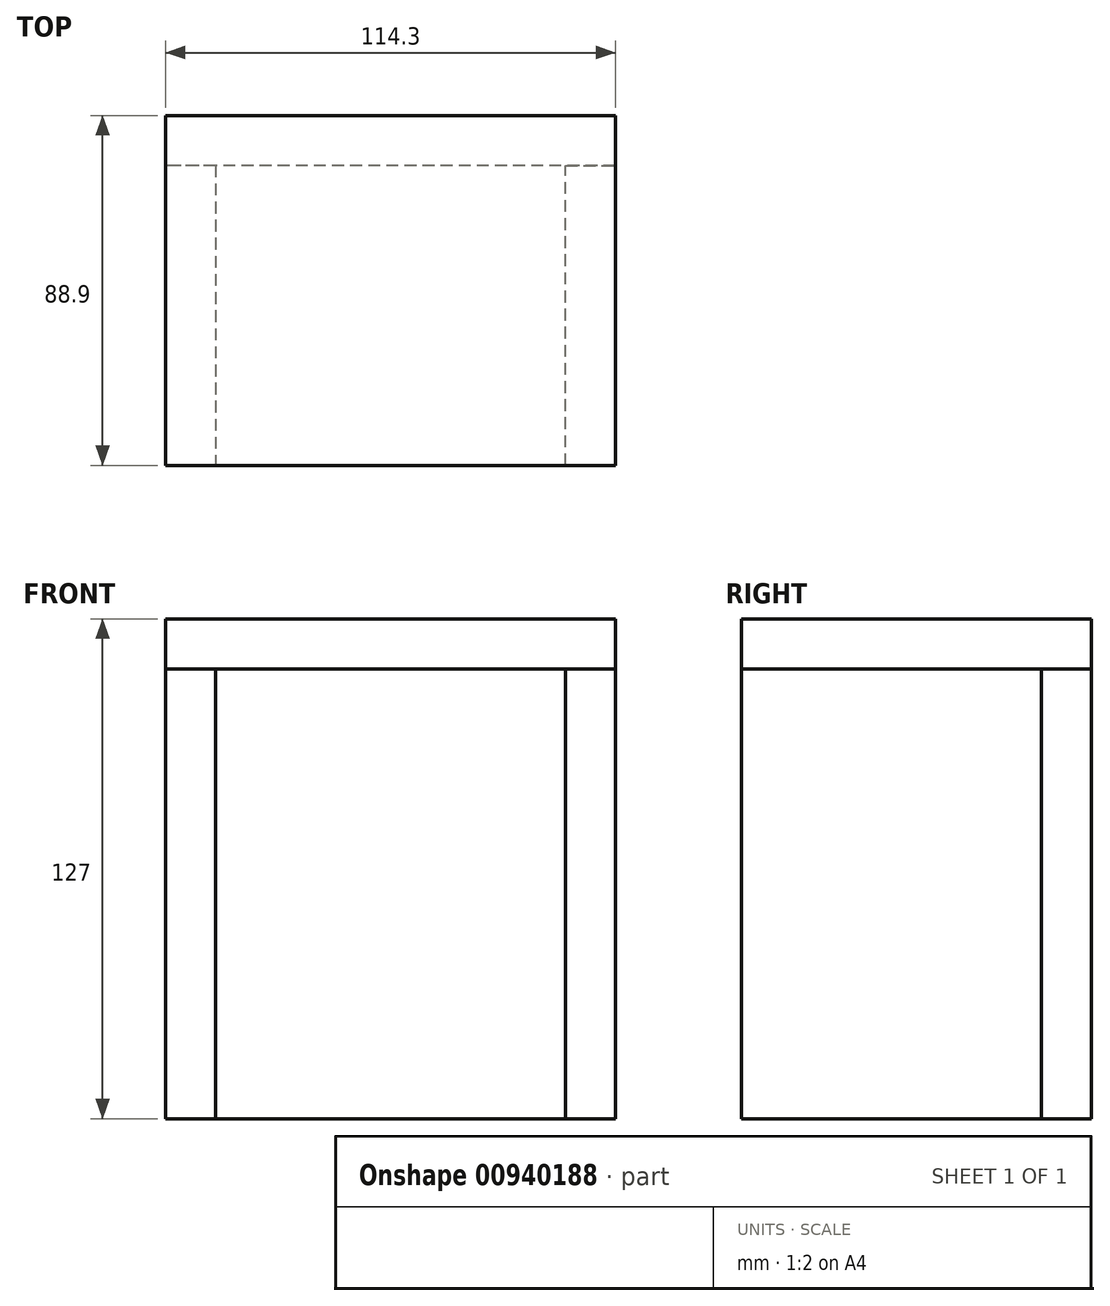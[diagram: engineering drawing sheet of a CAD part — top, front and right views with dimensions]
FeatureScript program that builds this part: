
annotation { "Feature Type Name" : "Feature", "Feature Type Description" : "" }
export const myFeature = defineFeature(function(context is Context, id is Id, definition is map)
    precondition{}
    {
        {
            var Q0;
            Q0=qCreatedBy(makeId("Top.planeOp"),FACE);
            var sketch = newSketch(context, id + "F0", { "sketchPlane" : qUnion([Q0])});
            skLineSegment(sketch, "E0.bottom", {"start": v(44.45, -38.1) * mm, "end": v(-44.45, -38.1) * mm, "construction": true});
            skLineSegment(sketch, "E0.top", {"start": v(44.45, 38.1) * mm, "end": v(-44.45, 38.1) * mm, "construction": true});
            skLineSegment(sketch, "E0.left", {"start": v(44.45, -38.1) * mm, "end": v(44.45, 38.1) * mm, "construction": true});
            skLineSegment(sketch, "E0.right", {"start": v(-44.45, -38.1) * mm, "end": v(-44.45, 38.1) * mm, "construction": true});
            skPoint(sketch, "E0.middle", {"position": v(0, 0) * mm});
            skLineSegment(sketch, "E1.bottom", {"start": v(-44.45, 38.1) * mm, "end": v(-57.15, 38.1) * mm});
            skLineSegment(sketch, "E1.top", {"start": v(-44.45, -38.1) * mm, "end": v(-57.15, -38.1) * mm});
            skLineSegment(sketch, "E1.left", {"start": v(-44.45, 38.1) * mm, "end": v(-44.45, -38.1) * mm});
            skLineSegment(sketch, "E1.right", {"start": v(-57.15, 38.1) * mm, "end": v(-57.15, -38.1) * mm});
            skLineSegment(sketch, "E2.bottom", {"start": v(44.45, -38.1) * mm, "end": v(57.15, -38.1) * mm});
            skLineSegment(sketch, "E2.top", {"start": v(44.45, 38.1) * mm, "end": v(57.15, 38.1) * mm});
            skLineSegment(sketch, "E2.left", {"start": v(44.45, -38.1) * mm, "end": v(44.45, 38.1) * mm});
            skLineSegment(sketch, "E2.right", {"start": v(57.15, -38.1) * mm, "end": v(57.15, 38.1) * mm});
            skLineSegment(sketch, "E3.bottom", {"start": v(-57.15, 38.1) * mm, "end": v(57.15, 38.1) * mm});
            skLineSegment(sketch, "E3.top", {"start": v(-57.15, 50.8) * mm, "end": v(57.15, 50.8) * mm});
            skLineSegment(sketch, "E3.left", {"start": v(-57.15, 38.1) * mm, "end": v(-57.15, 50.8) * mm});
            skLineSegment(sketch, "E3.right", {"start": v(57.15, 38.1) * mm, "end": v(57.15, 50.8) * mm});
            skSolve(sketch);
        }
        {
            var Q0;
            Q0=makeQuery(id+"F0.imprint","IMPRINT",FACE,{"disambiguationData":[TD([[makeQuery(id+"F0.imprint","IMPRINT",EDGE,{"derivedFrom":sQuery(id+"F0.wireOp",EDGE,"E1.top")}),-1.0]])]});
            var Q1;
            Q1=makeQuery(id+"F0.imprint","IMPRINT",FACE,{"disambiguationData":[TD([[makeQuery(id+"F0.imprint","IMPRINT",EDGE,{"derivedFrom":sQuery(id+"F0.wireOp",EDGE,"E2.bottom")}),1.0]])]});
            extrude(context, id + "F1", {"entities" : qUnion([Q0, Q1]), "endBound" : BoundingType.SYMMETRIC, "depth" : 114.3 * mm, "offsetDistance" : 25.4 * mm});
        }
        {
            var Q0;
            Q0=makeQuery(id+"F0.imprint","IMPRINT",FACE,{"disambiguationData":[TD([[makeQuery(id+"F0.imprint","IMPRINT",EDGE,{"derivedFrom":sQuery(id+"F0.wireOp",EDGE,"E3.top")}),-1.0]])]});
            extrude(context, id + "F2", {"entities" : qUnion([Q0]), "endBound" : BoundingType.SYMMETRIC, "depth" : 114.3 * mm, "offsetDistance" : 25.4 * mm});
        }
        {
            var Q0;
            Q0=makeQuery(id+"F2.opExtrude","CAP_FACE",FACE,{"disambiguationData":[OSD([sQuery(id+"F0.wireOp",EDGE,"E3.bottom"),sQuery(id+"F0.wireOp",EDGE,"E3.top"),sQuery(id+"F0.wireOp",EDGE,"E3.left"),sQuery(id+"F0.wireOp",EDGE,"E3.right")])],"isStart":false});
            var sketch = newSketch(context, id + "F3", { "sketchPlane" : qUnion([Q0])});
            skLineSegment(sketch, "E4.bottom", {"start": v(-57.15, 50.8) * mm, "end": v(57.15, 50.8) * mm});
            skLineSegment(sketch, "E4.top", {"start": v(-57.15, -38.1) * mm, "end": v(57.15, -38.1) * mm});
            skLineSegment(sketch, "E4.left", {"start": v(-57.15, 50.8) * mm, "end": v(-57.15, -38.1) * mm});
            skLineSegment(sketch, "E4.right", {"start": v(57.15, 50.8) * mm, "end": v(57.15, -38.1) * mm});
            skSolve(sketch);
        }
        {
            var Q0;
            Q0 = qSketchRegion(id + "F3", true);
            extrude(context, id + "F4", {"entities" : qUnion([Q0]), "depth" : 12.7 * mm, "offsetDistance" : 25.4 * mm});
        }
    });
